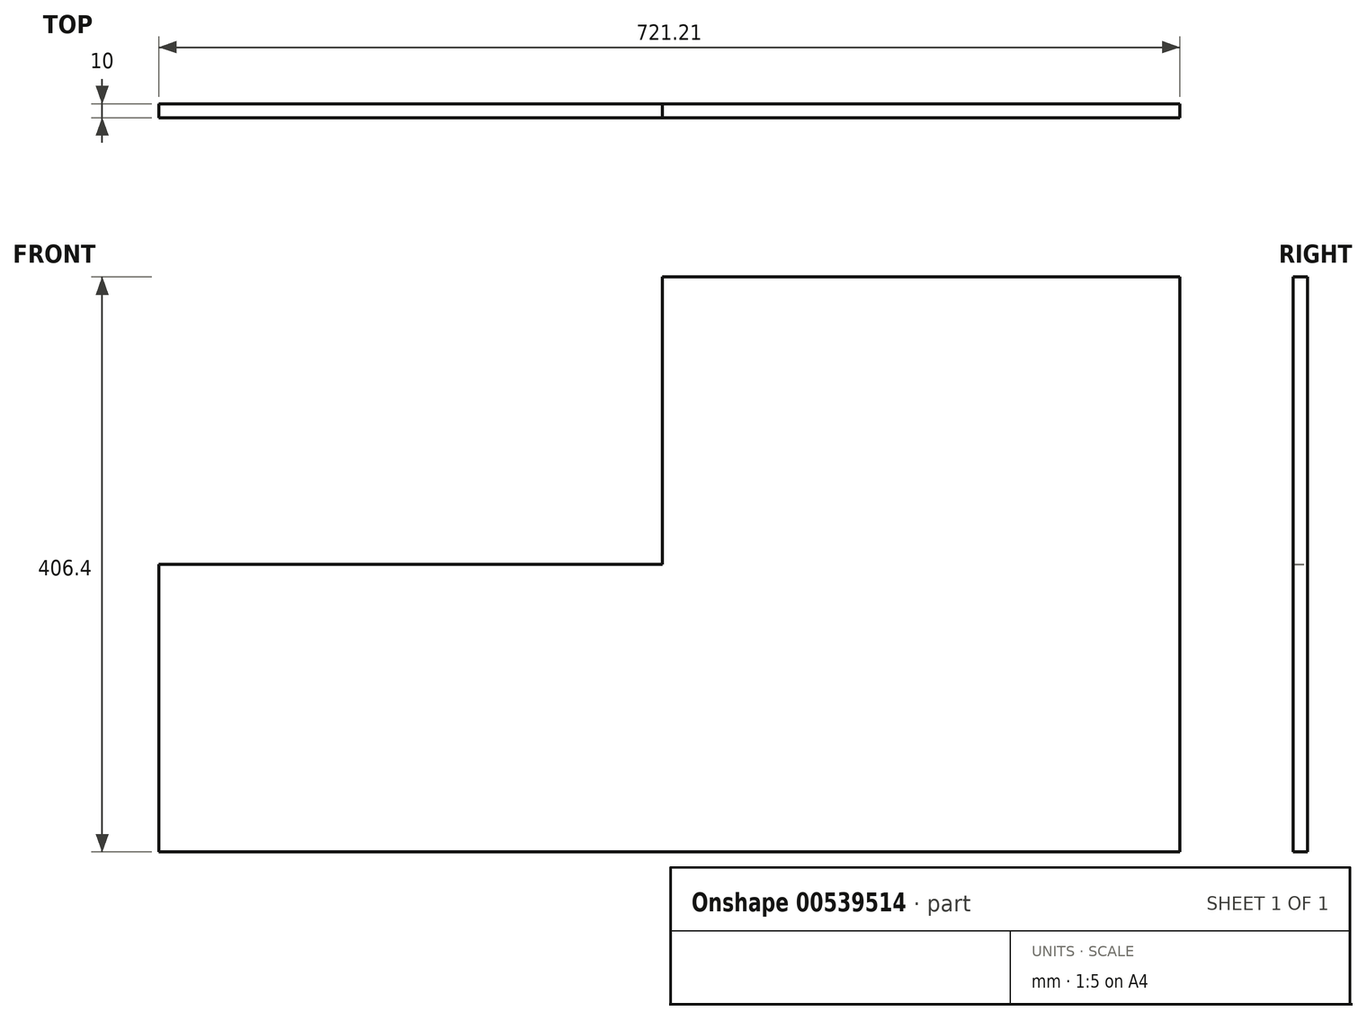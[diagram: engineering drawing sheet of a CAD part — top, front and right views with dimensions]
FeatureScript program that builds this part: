
annotation { "Feature Type Name" : "Feature", "Feature Type Description" : "" }
export const myFeature = defineFeature(function(context is Context, id is Id, definition is map)
    precondition{}
    {
        {
            var Q0;
            Q0=qCreatedBy(makeId("Front.planeOp"),FACE);
            var sketch = newSketch(context, id + "F0", { "sketchPlane" : qUnion([Q0])});
            skLineSegment(sketch, "E0", {"start": v(256.5, 237.91) * mm, "end": v(256.5, 441.11) * mm});
            skLineSegment(sketch, "E1", {"start": v(256.5, 441.11) * mm, "end": v(612.1, 441.11) * mm});
            skLineSegment(sketch, "E2", {"start": v(612.1, 441.11) * mm, "end": v(612.1, 644.31) * mm});
            skLineSegment(sketch, "E3", {"start": v(612.1, 644.31) * mm, "end": v(977.71, 644.31) * mm});
            skPoint(sketch, "E4.end.orphan", {"position": v(2.5, 34.71) * mm});
            skPoint(sketch, "E5.end.orphan", {"position": v(764.5, 34.71) * mm});
            skLineSegment(sketch, "E6", {"start": v(256.5, 237.91) * mm, "end": v(977.71, 237.91) * mm});
            skLineSegment(sketch, "E7", {"start": v(977.71, 237.91) * mm, "end": v(977.71, 644.31) * mm});
            skSolve(sketch);
        }
        {
            var Q0;
            Q0=makeQuery(id+"F0.imprint","IMPRINT",FACE,{"disambiguationData":[TD([[makeQuery(id+"F0.imprint","IMPRINT",EDGE,{"derivedFrom":sQuery(id+"F0.wireOp",EDGE,"xRCw6fde-mVwW-N1nc-w45f-0OqknuG21qwN")}),-1.0]])]});
            var Q1;
            Q1=makeQuery(id+"F0.imprint","IMPRINT",FACE,{"disambiguationData":[TD([[makeQuery(id+"F0.imprint","IMPRINT",EDGE,{"derivedFrom":sQuery(id+"F0.wireOp",EDGE,"E0")}),-1.0]])]});
            extrude(context, id + "F1", {"entities" : qUnion([Q0, Q1]), "depth" : 10 * mm, "offsetDistance" : 25.4 * mm});
        }
    });
